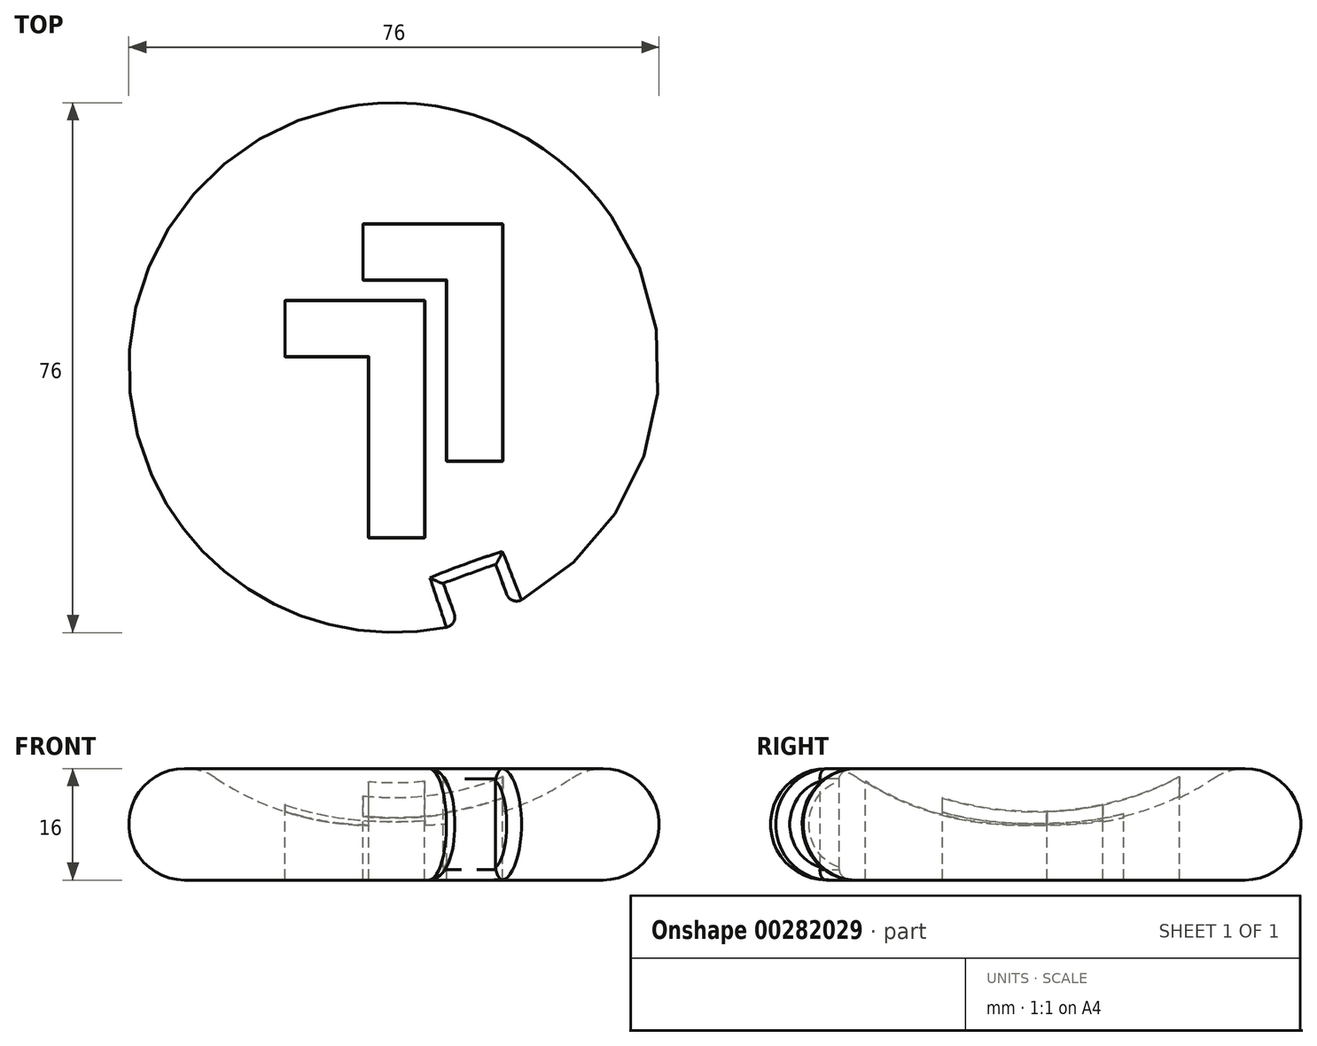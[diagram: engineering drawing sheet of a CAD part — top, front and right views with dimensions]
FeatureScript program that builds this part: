
annotation { "Feature Type Name" : "Feature", "Feature Type Description" : "" }
export const myFeature = defineFeature(function(context is Context, id is Id, definition is map)
    precondition{}
    {
        {
            var Q0;
            Q0=qCreatedBy(makeId("Top.planeOp"),FACE);
            var sketch = newSketch(context, id + "F0", { "sketchPlane" : qUnion([Q0])});
            skArc(sketch, "E0", {"start": v(-12.77, 7.32) * mm, "mid": v(-6.67, 4.58) * mm, "end": v(0, 4) * mm});
            skLineSegment(sketch, "E1", {"start": v(-15, 0) * mm, "end": v(0, 0) * mm});
            skArc(sketch, "E2", {"start": v(-12.77, 7.32) * mm, "mid": v(-18.83, 5.16) * mm, "end": v(-15, 0) * mm});
            skLineSegment(sketch, "E3", {"start": v(0, 0) * mm, "end": v(0, 4) * mm});
            skSolve(sketch);
        }
        {
            var Q0;
            Q0=makeQuery(id+"F0.imprint","IMPRINT",FACE,{"disambiguationData":[TD([[makeQuery(id+"F0.imprint","IMPRINT",EDGE,{"derivedFrom":sQuery(id+"F0.wireOp",EDGE,"E0")}),-1.0]])]});
            var Q1;
            Q1=sQuery(id+"F0.wireOp",EDGE,"E3");
            revolve(context, id + "F1", {"entities" : qUnion([Q0]), "axis" : qUnion([Q1]), "revolveType" : RevolveType.FULL});
        }
        {
            var Q0;
            Q0=qCreatedBy(makeId("Front.planeOp"),FACE);
            cPlane(context, id + "F2", {"entities" : qUnion([Q0]), "cplaneType" : CPlaneType.OFFSET, "offset" : 20 * mm, "oppositeDirection" : true, "width" : 150 * mm, "height" : 150 * mm});
        }
        {
            var Q0;
            Q0=qCreatedBy(id+"F2.planeOp",FACE);
            var sketch = newSketch(context, id + "F3", { "sketchPlane" : qUnion([Q0])});
            skLineSegment(sketch, "E4", {"start": v(6.8, 5.7) * mm, "end": v(6.8, -9.3) * mm});
            skLineSegment(sketch, "E5", {"start": v(6.8, -9.3) * mm, "end": v(-1.2, -9.3) * mm});
            skLineSegment(sketch, "E6", {"start": v(-1.2, -9.3) * mm, "end": v(-1.2, -7.3) * mm});
            skLineSegment(sketch, "E7", {"start": v(-1.2, -7.3) * mm, "end": v(4.8, -7.3) * mm});
            skLineSegment(sketch, "E8", {"start": v(4.8, -7.3) * mm, "end": v(4.8, 5.7) * mm});
            skLineSegment(sketch, "E9", {"start": v(4.8, 5.7) * mm, "end": v(6.8, 5.7) * mm});
            skLineSegment(sketch, "E10.0", {"start": v(-2.2, -6.3) * mm, "end": v(3.8, -6.3) * mm});
            skLineSegment(sketch, "E10.1", {"start": v(3.8, 6.7) * mm, "end": v(7.8, 6.7) * mm});
            skLineSegment(sketch, "E10.2", {"start": v(7.8, 6.7) * mm, "end": v(7.8, -10.3) * mm});
            skLineSegment(sketch, "E10.3", {"start": v(3.8, -6.3) * mm, "end": v(3.8, 6.7) * mm});
            skLineSegment(sketch, "E10.4", {"start": v(7.8, -10.3) * mm, "end": v(-2.2, -10.3) * mm});
            skLineSegment(sketch, "E10.5", {"start": v(-2.2, -10.3) * mm, "end": v(-2.2, -6.3) * mm});
            skLineSegment(sketch, "E11", {"start": v(1.2, 11.2) * mm, "end": v(1.2, -3.8) * mm});
            skLineSegment(sketch, "E12", {"start": v(1.2, -3.8) * mm, "end": v(-6.8, -3.8) * mm});
            skLineSegment(sketch, "E13", {"start": v(-6.8, -3.8) * mm, "end": v(-6.8, -1.8) * mm});
            skLineSegment(sketch, "E14", {"start": v(-6.8, -1.8) * mm, "end": v(-0.8, -1.8) * mm});
            skLineSegment(sketch, "E15", {"start": v(-0.8, -1.8) * mm, "end": v(-0.8, 11.2) * mm});
            skLineSegment(sketch, "E16", {"start": v(-0.8, 11.2) * mm, "end": v(1.2, 11.2) * mm});
            skLineSegment(sketch, "E17.0", {"start": v(-7.8, -0.8) * mm, "end": v(-1.8, -0.8) * mm});
            skLineSegment(sketch, "E17.1", {"start": v(-1.8, 12.2) * mm, "end": v(2.2, 12.2) * mm});
            skLineSegment(sketch, "E17.2", {"start": v(2.2, 12.2) * mm, "end": v(2.2, -4.8) * mm});
            skLineSegment(sketch, "E17.3", {"start": v(-1.8, -0.8) * mm, "end": v(-1.8, 12.2) * mm});
            skLineSegment(sketch, "E17.4", {"start": v(2.2, -4.8) * mm, "end": v(-7.8, -4.8) * mm});
            skLineSegment(sketch, "E17.5", {"start": v(-7.8, -4.8) * mm, "end": v(-7.8, -0.8) * mm});
            skSolve(sketch);
        }
        {
            var Q0;
            Q0=makeQuery(id+"F3.imprint","IMPRINT",FACE,{"disambiguationData":[TD([[makeQuery(id+"F3.imprint","IMPRINT",EDGE,{"derivedFrom":sQuery(id+"F3.wireOp",EDGE,"E4")}),1.0]])]});
            var Q1;
            Q1=makeQuery(id+"F3.imprint","IMPRINT",FACE,{"disambiguationData":[TD([[makeQuery(id+"F3.imprint","IMPRINT",EDGE,{"derivedFrom":sQuery(id+"F3.wireOp",EDGE,"E11")}),1.0]])]});
            var Q2;
            Q2=makeQuery(id+"F3.imprint","IMPRINT",FACE,{"disambiguationData":[TD([[makeQuery(id+"F3.imprint","IMPRINT",EDGE,{"derivedFrom":sQuery(id+"F3.wireOp",EDGE,"E11")}),-1.0]])]});
            var Q3;
            Q3=makeQuery(id+"F3.imprint","IMPRINT",FACE,{"disambiguationData":[TD([[makeQuery(id+"F3.imprint","IMPRINT",EDGE,{"derivedFrom":sQuery(id+"F3.wireOp",EDGE,"E4")}),-1.0]])]});
            extrude(context, id + "F4", {"entities" : qUnion([Q0, Q1, Q2, Q3]), "operationType" : NewBodyOperationType.REMOVE, "depth" : 25 * mm});
        }
        {
            var Q0;
            Q0=makeQuery(id+"F4.boolean.opBoolean","INTERSECT",EDGE,{"derivedFrom":[makeQuery(id+"F1.opRevolve","SWEPT_FACE",FACE,{"disambiguationData":[OSD([sQuery(id+"F0.wireOp",EDGE,"E1")])]}),makeQuery(id+"F4.opExtrude","SWEPT_FACE",FACE,{"disambiguationData":[OSD([sQuery(id+"F3.wireOp",EDGE,"E10.2")])]})]});
            var Q1;
            Q1=makeQuery(id+"F4.boolean.opBoolean","INTERSECT",EDGE,{"derivedFrom":[makeQuery(id+"F1.opRevolve","SWEPT_FACE",FACE,{"disambiguationData":[OSD([sQuery(id+"F0.wireOp",EDGE,"E1")])]}),makeQuery(id+"F4.opExtrude","SWEPT_FACE",FACE,{"disambiguationData":[OSD([sQuery(id+"F3.wireOp",EDGE,"E10.4")])]})]});
            var Q2;
            Q2=makeQuery(id+"F4.boolean.opBoolean","INTERSECT",EDGE,{"derivedFrom":[makeQuery(id+"F1.opRevolve","SWEPT_FACE",FACE,{"disambiguationData":[OSD([sQuery(id+"F0.wireOp",EDGE,"E1")])]}),makeQuery(id+"F4.opExtrude","SWEPT_FACE",FACE,{"disambiguationData":[OSD([sQuery(id+"F3.wireOp",EDGE,"E10.5")])]})]});
            var Q3;
            Q3=makeQuery(id+"F4.boolean.opBoolean","INTERSECT",EDGE,{"derivedFrom":[makeQuery(id+"F1.opRevolve","SWEPT_FACE",FACE,{"disambiguationData":[OSD([sQuery(id+"F0.wireOp",EDGE,"E1")])]}),makeQuery(id+"F4.opExtrude","SWEPT_FACE",FACE,{"disambiguationData":[OSD([sQuery(id+"F3.wireOp",EDGE,"E10.0")])]})]});
            var Q4;
            Q4=makeQuery(id+"F4.boolean.opBoolean","INTERSECT",EDGE,{"derivedFrom":[makeQuery(id+"F1.opRevolve","SWEPT_FACE",FACE,{"disambiguationData":[OSD([sQuery(id+"F0.wireOp",EDGE,"E1")])]}),makeQuery(id+"F4.opExtrude","SWEPT_FACE",FACE,{"disambiguationData":[OSD([sQuery(id+"F3.wireOp",EDGE,"E10.3")])]})]});
            var Q5;
            Q5=makeQuery(id+"F4.boolean.opBoolean","INTERSECT",EDGE,{"derivedFrom":[makeQuery(id+"F1.opRevolve","SWEPT_FACE",FACE,{"disambiguationData":[OSD([sQuery(id+"F0.wireOp",EDGE,"E1")])]}),makeQuery(id+"F4.opExtrude","SWEPT_FACE",FACE,{"disambiguationData":[OSD([sQuery(id+"F3.wireOp",EDGE,"E10.1")])]})]});
            var Q6;
            Q6=makeQuery(id+"F4.boolean.opBoolean","INTERSECT",EDGE,{"derivedFrom":[makeQuery(id+"F1.opRevolve","SWEPT_FACE",FACE,{"disambiguationData":[OSD([sQuery(id+"F0.wireOp",EDGE,"E1")])]}),makeQuery(id+"F4.opExtrude","SWEPT_FACE",FACE,{"disambiguationData":[OSD([sQuery(id+"F3.wireOp",EDGE,"E17.2")])]})]});
            var Q7;
            Q7=makeQuery(id+"F4.boolean.opBoolean","COPY",FACE,{"derivedFrom":makeQuery(id+"F4.opExtrude","SWEPT_FACE",FACE,{"disambiguationData":[OSD([sQuery(id+"F3.wireOp",EDGE,"E17.2")])]})});
            var Q8;
            Q8=makeQuery(id+"F4.boolean.opBoolean","COPY",FACE,{"derivedFrom":makeQuery(id+"F4.opExtrude","SWEPT_FACE",FACE,{"disambiguationData":[OSD([sQuery(id+"F3.wireOp",EDGE,"E17.4")])]})});
            var Q9;
            Q9=makeQuery(id+"F4.boolean.opBoolean","COPY",FACE,{"derivedFrom":makeQuery(id+"F4.opExtrude","SWEPT_FACE",FACE,{"disambiguationData":[OSD([sQuery(id+"F3.wireOp",EDGE,"E17.5")])]})});
            var Q10;
            Q10=makeQuery(id+"F4.boolean.opBoolean","COPY",FACE,{"derivedFrom":makeQuery(id+"F4.opExtrude","SWEPT_FACE",FACE,{"disambiguationData":[OSD([sQuery(id+"F3.wireOp",EDGE,"E17.0")])]})});
            var Q11;
            Q11=makeQuery(id+"F4.boolean.opBoolean","COPY",FACE,{"derivedFrom":makeQuery(id+"F4.opExtrude","SWEPT_FACE",FACE,{"disambiguationData":[OSD([sQuery(id+"F3.wireOp",EDGE,"E17.3")])]})});
            var Q12;
            Q12=makeQuery(id+"F4.boolean.opBoolean","COPY",FACE,{"derivedFrom":makeQuery(id+"F4.opExtrude","SWEPT_FACE",FACE,{"disambiguationData":[OSD([sQuery(id+"F3.wireOp",EDGE,"E17.1")])]})});
            var Q13;
            Q13=makeQuery(id+"F4.boolean.opBoolean","COPY",FACE,{"derivedFrom":makeQuery(id+"F4.opExtrude","SWEPT_FACE",FACE,{"disambiguationData":[OSD([sQuery(id+"F3.wireOp",EDGE,"E10.4")])]})});
            var Q14;
            Q14=makeQuery(id+"F4.boolean.opBoolean","COPY",FACE,{"derivedFrom":makeQuery(id+"F4.opExtrude","SWEPT_FACE",FACE,{"disambiguationData":[OSD([sQuery(id+"F3.wireOp",EDGE,"E10.2")])]})});
            var Q15;
            Q15=makeQuery(id+"F4.boolean.opBoolean","COPY",FACE,{"derivedFrom":makeQuery(id+"F4.opExtrude","SWEPT_FACE",FACE,{"disambiguationData":[OSD([sQuery(id+"F3.wireOp",EDGE,"E10.5")])]})});
            var Q16;
            Q16=makeQuery(id+"F4.boolean.opBoolean","COPY",FACE,{"derivedFrom":makeQuery(id+"F4.opExtrude","SWEPT_FACE",FACE,{"disambiguationData":[OSD([sQuery(id+"F3.wireOp",EDGE,"E10.0")])]})});
            var Q17;
            Q17=makeQuery(id+"F4.boolean.opBoolean","COPY",FACE,{"derivedFrom":makeQuery(id+"F4.opExtrude","SWEPT_FACE",FACE,{"disambiguationData":[OSD([sQuery(id+"F3.wireOp",EDGE,"E10.3")])]})});
            var Q18;
            Q18=makeQuery(id+"F4.boolean.opBoolean","COPY",FACE,{"derivedFrom":makeQuery(id+"F4.opExtrude","SWEPT_FACE",FACE,{"disambiguationData":[OSD([sQuery(id+"F3.wireOp",EDGE,"E10.1")])]})});
            fillet(context, id + "F5", {"entities" : qUnion([Q0, Q1, Q2, Q3, Q4, Q5, Q6, Q7, Q8, Q9, Q10, Q11, Q12, Q13, Q14, Q15, Q16, Q17, Q18]), "radius" : 0.02 * mm, "tangentPropagation" : true, "allowEdgeOverflow" : false});
        }
        {
            var Q0;
            Q0=qCreatedBy(id+"F2.planeOp",FACE);
            var sketch = newSketch(context, id + "F6", { "sketchPlane" : qUnion([Q0])});
            skLineSegment(sketch, "E18.bottom", {"start": v(8.66, 17.85) * mm, "end": v(4.9, 19.22) * mm});
            skLineSegment(sketch, "E18.top", {"start": v(7.3, 14.1) * mm, "end": v(3.54, 15.46) * mm});
            skLineSegment(sketch, "E18.left", {"start": v(8.66, 17.85) * mm, "end": v(7.3, 14.1) * mm});
            skLineSegment(sketch, "E18.right", {"start": v(4.9, 19.22) * mm, "end": v(3.54, 15.46) * mm});
            skSolve(sketch);
        }
        {
            var Q0;
            Q0 = qSketchRegion(id + "F6", true);
            extrude(context, id + "F7", {"entities" : qUnion([Q0]), "operationType" : NewBodyOperationType.REMOVE, "depth" : 25 * mm});
        }
        {
            var Q0;
            Q0=makeQuery(id+"F7.boolean.opBoolean","INTERSECT",EDGE,{"derivedFrom":[makeQuery(id+"F1.opRevolve","SWEPT_FACE",FACE,{"disambiguationData":[OSD([sQuery(id+"F0.wireOp",EDGE,"E2")])]}),makeQuery(id+"F7.opExtrude","SWEPT_FACE",FACE,{"disambiguationData":[OSD([sQuery(id+"F6.wireOp",EDGE,"E18.right")])]})]});
            var Q1;
            Q1=makeQuery(id+"F7.boolean.opBoolean","INTERSECT",EDGE,{"derivedFrom":[makeQuery(id+"F1.opRevolve","SWEPT_FACE",FACE,{"disambiguationData":[OSD([sQuery(id+"F0.wireOp",EDGE,"E2")])]}),makeQuery(id+"F7.opExtrude","SWEPT_FACE",FACE,{"disambiguationData":[OSD([sQuery(id+"F6.wireOp",EDGE,"E18.left")])]})]});
            var Q2;
            Q2=makeQuery(id+"F7.boolean.opBoolean","INTERSECT",EDGE,{"disambiguationData":[OD(0.0)],"derivedFrom":[makeQuery(id+"F1.opRevolve","SWEPT_FACE",FACE,{"disambiguationData":[OSD([sQuery(id+"F0.wireOp",EDGE,"E2")])]}),makeQuery(id+"F7.opExtrude","SWEPT_FACE",FACE,{"disambiguationData":[OSD([sQuery(id+"F6.wireOp",EDGE,"E18.top")])]})]});
            var Q3;
            Q3=makeQuery(id+"F7.boolean.opBoolean","INTERSECT",EDGE,{"disambiguationData":[OD(1.0)],"derivedFrom":[makeQuery(id+"F1.opRevolve","SWEPT_FACE",FACE,{"disambiguationData":[OSD([sQuery(id+"F0.wireOp",EDGE,"E2")])]}),makeQuery(id+"F7.opExtrude","SWEPT_FACE",FACE,{"disambiguationData":[OSD([sQuery(id+"F6.wireOp",EDGE,"E18.top")])]})]});
            fillet(context, id + "F8", {"entities" : qUnion([Q0, Q1, Q2, Q3]), "radius" : .75 * mm, "tangentPropagation" : true, "allowEdgeOverflow" : false});
        }
        {
            var Q0;
            Q0=qCreatedBy(makeId("Top.planeOp"),FACE);
            var sketch = newSketch(context, id + "F9", { "sketchPlane" : qUnion([Q0])});
            skCircle(sketch, "E19", {"center": v(-11.64, 3.43) * mm, "radius": 2.63 * mm});
            skSolve(sketch);
        }
        {
            var Q0;
            Q0=sQuery(id+"F9.wireOp",EDGE,"E19");
            var Q1;
            Q1=sQuery(id+"F0.wireOp",EDGE,"E3");
            revolve(context, id + "F10", {"bodyType" : ToolBodyType.SURFACE, "surfaceEntities" : qUnion([Q0]), "axis" : qUnion([Q1]), "revolveType" : RevolveType.FULL});
        }
        {
            var Q0;
            Q0=makeQuery(id+"F1.opRevolve","SWEPT_BODY",BODY,{"disambiguationData":[OSD([sQuery(id+"F0.wireOp",EDGE,"E0"),sQuery(id+"F0.wireOp",EDGE,"E1"),sQuery(id+"F0.wireOp",EDGE,"E2"),sQuery(id+"F0.wireOp",EDGE,"E3")])]});
            var Q1;
            Q1=makeQuery(id+"F10.opRevolve","SWEPT_BODY",BODY,{"disambiguationData":[OSD([sQuery(id+"F9.wireOp",EDGE,"E19")])]});
            var Q2;
            Q2=sQuery(id+"F0.wireOp",VERTEX,"E3.start");
            transform(context, id + "F11", {"entities" : qUnion([Q0, Q1]), "transformType" : TransformType.SCALE_UNIFORMLY, "scale" : 2, "scalePoint" : qUnion([Q2]), "makeCopy" : false});
        }
        {
            var Q0;
            Q0=makeQuery(id+"F1.opRevolve","SWEPT_BODY",BODY,{"disambiguationData":[OSD([sQuery(id+"F0.wireOp",EDGE,"E0"),sQuery(id+"F0.wireOp",EDGE,"E1"),sQuery(id+"F0.wireOp",EDGE,"E2"),sQuery(id+"F0.wireOp",EDGE,"E3")])]});
            var Q1;
            Q1=makeQuery(id+"F10.opRevolve","SWEPT_BODY",BODY,{"disambiguationData":[OSD([sQuery(id+"F9.wireOp",EDGE,"E19")])]});
            var Q2;
            Q2=sQuery(id+"F0.wireOp",EDGE,"E1");
            transform(context, id + "F12", {"entities" : qUnion([Q0, Q1]), "transformType" : TransformType.ROTATION, "transformAxis" : qUnion([Q2]), "angle" : 90 * degree, "makeCopy" : false});
        }
    });
